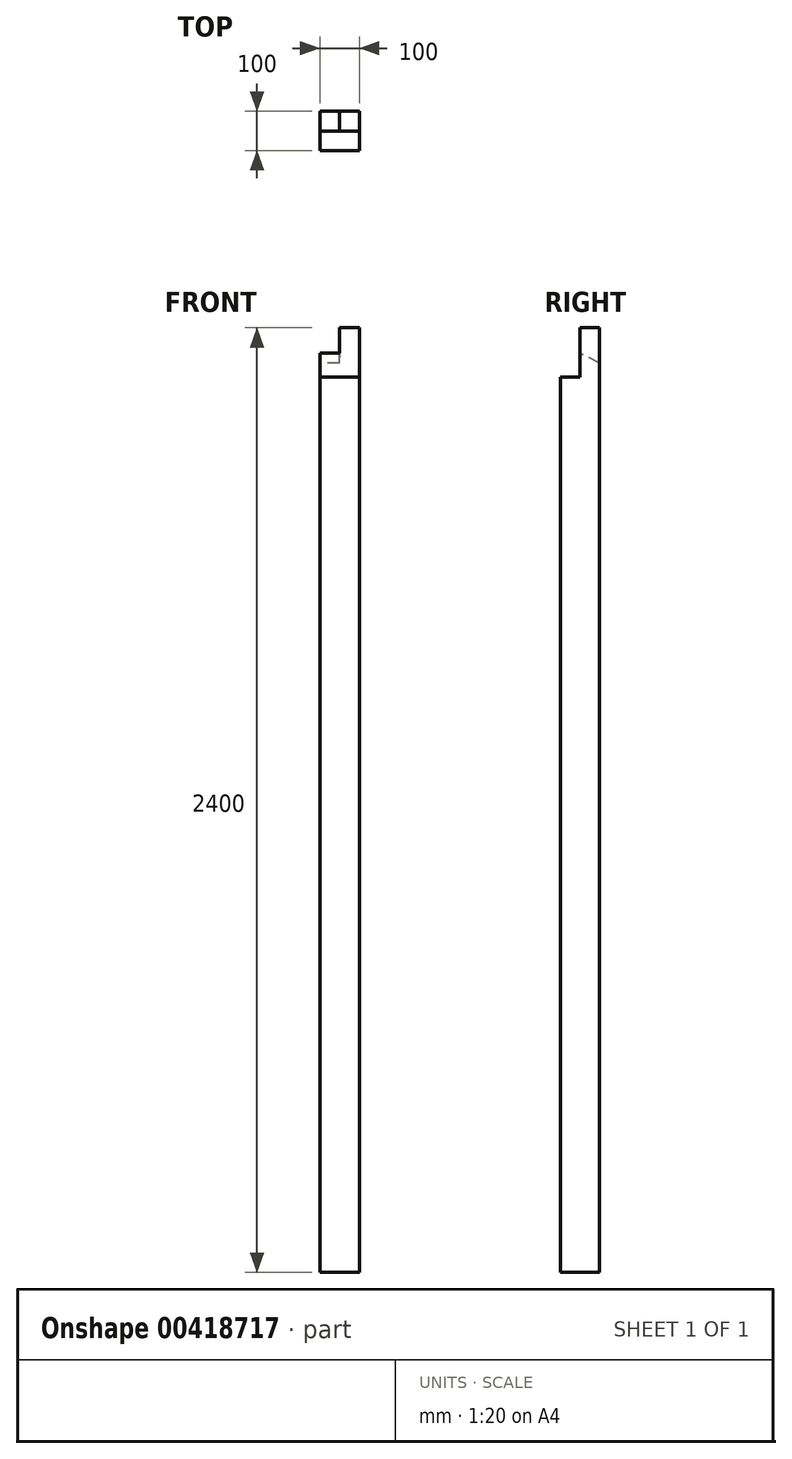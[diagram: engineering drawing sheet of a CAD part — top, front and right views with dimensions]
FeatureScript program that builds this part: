
annotation { "Feature Type Name" : "Feature", "Feature Type Description" : "" }
export const myFeature = defineFeature(function(context is Context, id is Id, definition is map)
    precondition{}
    {
        {
            var Q0;
            Q0=qCreatedBy(makeId("Top.planeOp"),FACE);
            var sketch = newSketch(context, id + "F0", { "sketchPlane" : qUnion([Q0])});
            skLineSegment(sketch, "E0.bottom", {"start": v(50, 50) * mm, "end": v(-50, 50) * mm});
            skLineSegment(sketch, "E0.top", {"start": v(50, -50) * mm, "end": v(-50, -50) * mm});
            skLineSegment(sketch, "E0.left", {"start": v(50, 50) * mm, "end": v(50, -50) * mm});
            skLineSegment(sketch, "E0.right", {"start": v(-50, 50) * mm, "end": v(-50, -50) * mm});
            skPoint(sketch, "E0.middle", {"position": v(0, 0) * mm});
            skSolve(sketch);
        }
        {
            var Q0;
            Q0 = qSketchRegion(id + "F0", true);
            extrude(context, id + "F1", {"entities" : qUnion([Q0]), "depth" : 2400 * mm});
        }
        {
            var Q0;
            Q0=qCreatedBy(makeId("Right.planeOp"),FACE);
            var sketch = newSketch(context, id + "F2", { "sketchPlane" : qUnion([Q0])});
            skLineSegment(sketch, "E1.bottom", {"start": v(-50, 2400) * mm, "end": v(0, 2400) * mm});
            skLineSegment(sketch, "E1.top", {"start": v(-50, 2275) * mm, "end": v(0, 2275) * mm});
            skLineSegment(sketch, "E1.left", {"start": v(-50, 2400) * mm, "end": v(-50, 2275) * mm});
            skLineSegment(sketch, "E1.right", {"start": v(0, 2400) * mm, "end": v(0, 2275) * mm});
            skSolve(sketch);
        }
        {
            var Q0;
            Q0 = qSketchRegion(id + "F2", true);
            extrude(context, id + "F3", {"entities" : qUnion([Q0]), "operationType" : NewBodyOperationType.REMOVE, "endBound" : BoundingType.UP_TO_NEXT, "oppositeDirection" : true, "depth" : 25 * mm, "hasSecondDirection" : true, "secondDirectionBound" : SecondDirectionBoundingType.UP_TO_NEXT, "secondDirectionOppositeDirection" : false, "secondDirectionDepth" : 25 * mm});
        }
        {
            var Q0;
            Q0=makeQuery(id+"F1.opExtrude","SWEPT_FACE",FACE,{"disambiguationData":[OSD([sQuery(id+"F0.wireOp",EDGE,"E0.right")])]});
            var sketch = newSketch(context, id + "F4", { "sketchPlane" : qUnion([Q0])});
            skLineSegment(sketch, "E2", {"start": v(-50, 2400) * mm, "end": v(-50, 2310.25) * mm});
            skLineSegment(sketch, "E3", {"start": v(-50, 2310.25) * mm, "end": v(0, 2335.25) * mm});
            skLineSegment(sketch, "E4", {"start": v(0, 2335.25) * mm, "end": v(0, 2400) * mm});
            skLineSegment(sketch, "E5", {"start": v(0, 2400) * mm, "end": v(-50, 2400) * mm});
            skSolve(sketch);
        }
        {
            var Q0;
            Q0 = qSketchRegion(id + "F4", true);
            extrude(context, id + "F5", {"entities" : qUnion([Q0]), "operationType" : NewBodyOperationType.REMOVE, "oppositeDirection" : true, "depth" : 50 * mm});
        }
    });
